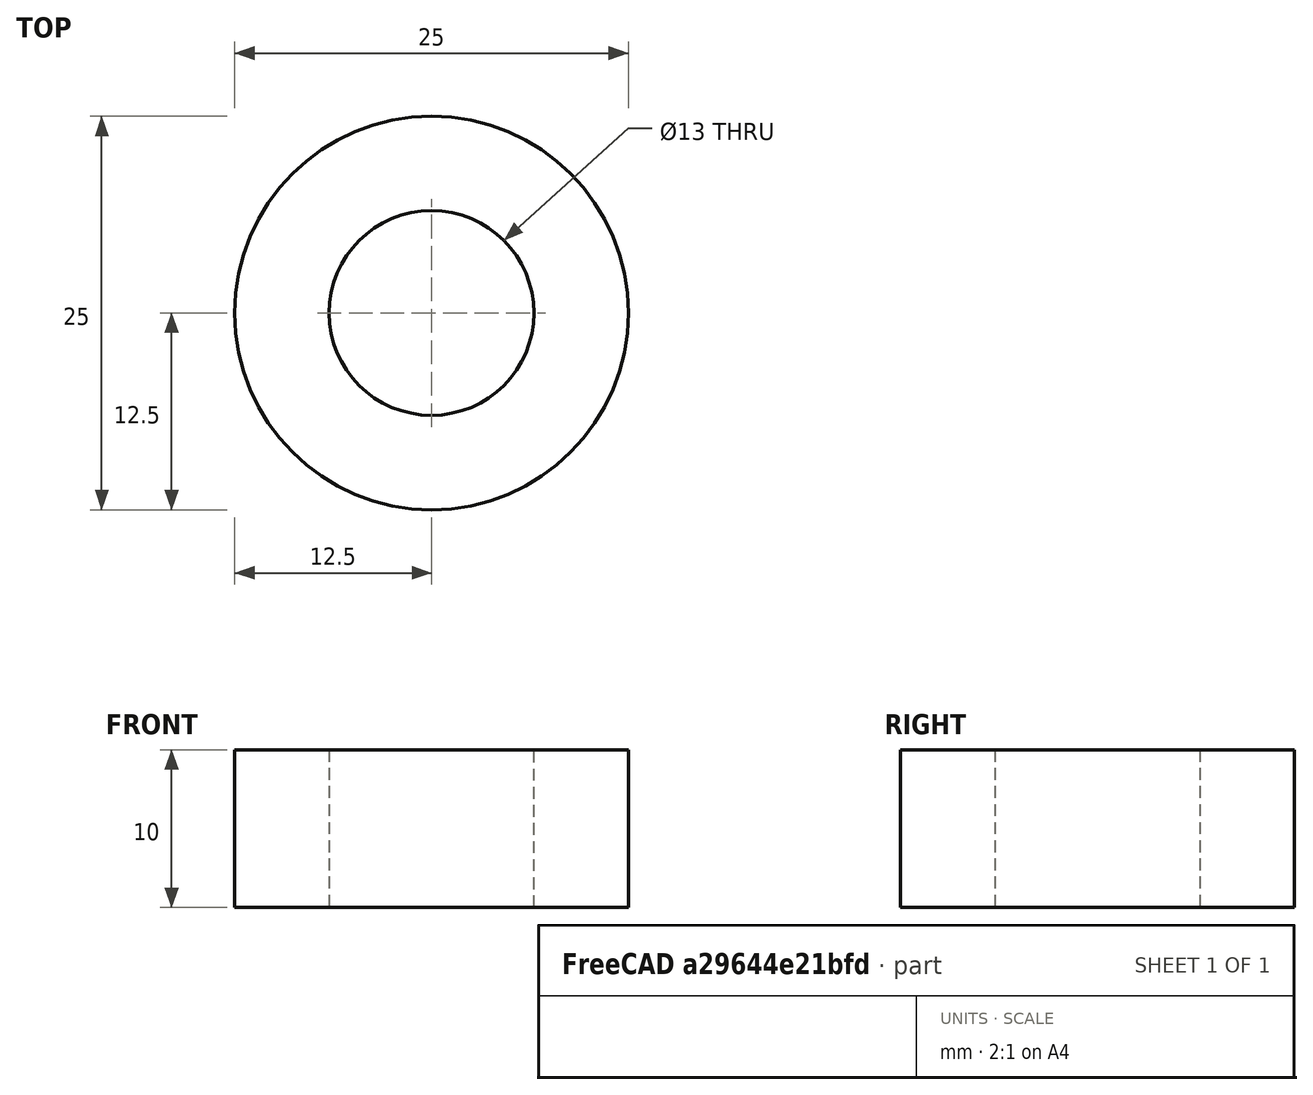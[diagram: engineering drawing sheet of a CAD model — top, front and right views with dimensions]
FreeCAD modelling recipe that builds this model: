
FCSTD DOCUMENT  (FreeCAD 0.20R29177 (Git))
Label: holePress6.5mm
License: All rights reserved
LicenseURL: http://en.wikipedia.org/wiki/All_rights_reserved
objects: Sketcher::SketchObject×1, PartDesign::Pad×1, PartDesign::Body×1
note: 4 computed .brp shape members not serialized (recipe doc carries the construction recipe); baked Part::Feature solids carry a one-line shape summary decoded from their .brp

FEATURE [Sketcher::SketchObject] Sketch
  FullyConstrained = true
  MapMode = 5
  Support = -> [XY_Plane]
  sketch-geometry (2):
    g0: Circle CenterX=0 CenterY=0 CenterZ=0 NormalX=0 NormalY=0 NormalZ=1 AngleXU=0 Radius=6.5
    g1: Circle CenterX=0 CenterY=0 CenterZ=0 NormalX=0 NormalY=0 NormalZ=1 AngleXU=0 Radius=12.5
  constraints (4):
    c: Coincident(g0,g-1)
    c: Radius(g0) = 6.5
    c: Coincident(g1,g0)
    c: Radius(g1) = 12.5
FEATURE [PartDesign::Pad] Pad
  Direction = (0,0,1)
  Length = 10
  Length2 = 10
  Profile = -> Sketch
  ReferenceAxis = -> Sketch [N_Axis]
  Type = 0
FEATURE [PartDesign::Body] Body
  Group = -> [Sketch,Pad]
  Origin = -> Origin
  Tip = -> Pad
